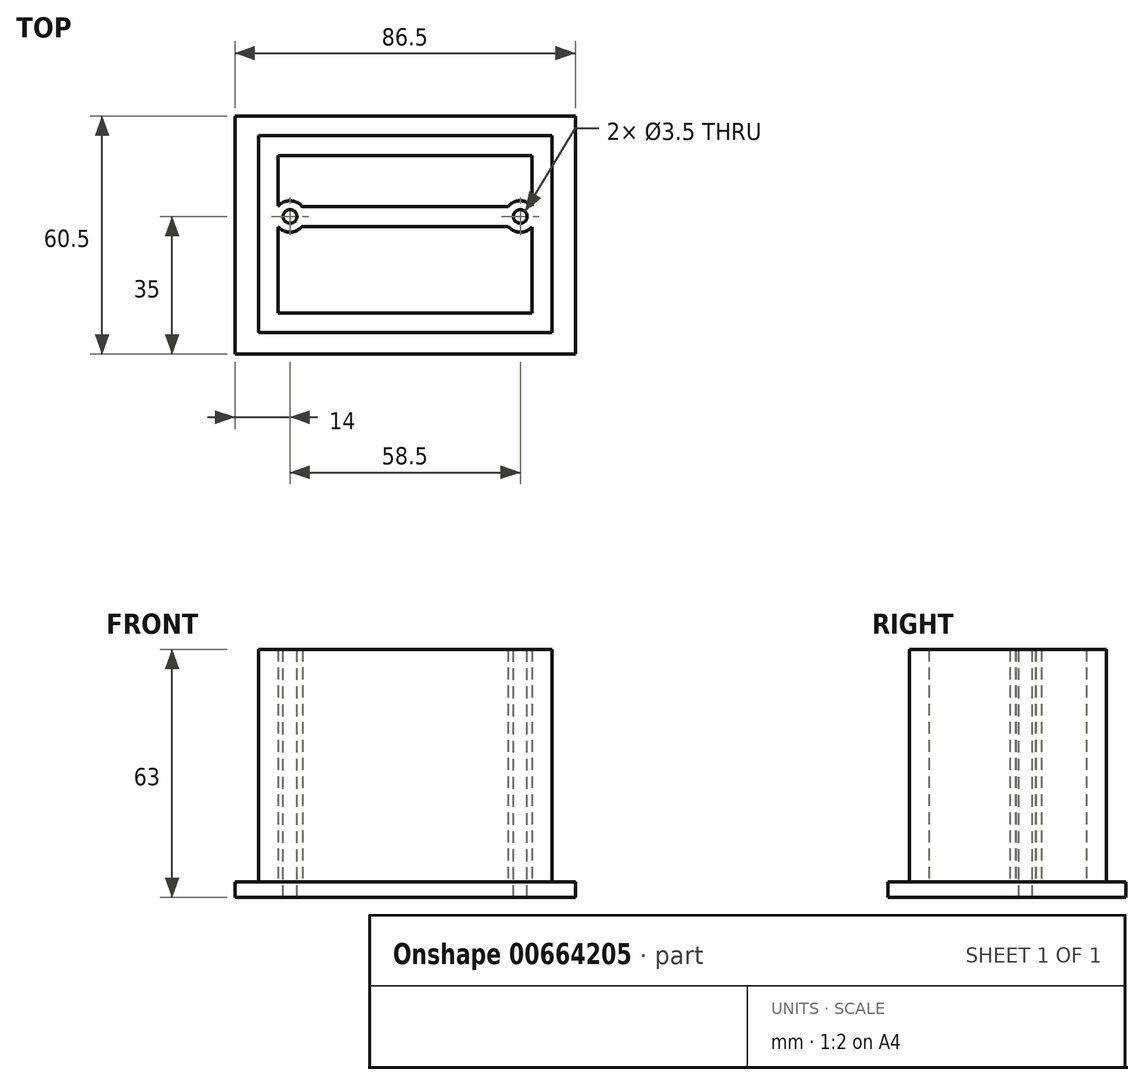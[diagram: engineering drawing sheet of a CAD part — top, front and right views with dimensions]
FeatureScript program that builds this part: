
annotation { "Feature Type Name" : "Feature", "Feature Type Description" : "" }
export const myFeature = defineFeature(function(context is Context, id is Id, definition is map)
    precondition{}
    {
        {
            var Q0;
            Q0=qCreatedBy(makeId("Top.planeOp"),FACE);
            var sketch = newSketch(context, id + "F0", { "sketchPlane" : qUnion([Q0])});
            skLineSegment(sketch, "E0.bottom", {"start": v(43.25, 30.25) * mm, "end": v(-43.25, 30.25) * mm});
            skLineSegment(sketch, "E0.top", {"start": v(43.25, -30.25) * mm, "end": v(-43.25, -30.25) * mm});
            skLineSegment(sketch, "E0.left", {"start": v(43.25, 30.25) * mm, "end": v(43.25, -30.25) * mm});
            skLineSegment(sketch, "E0.right", {"start": v(-43.25, 30.25) * mm, "end": v(-43.25, -30.25) * mm});
            skPoint(sketch, "E0.middle", {"position": v(0, 0) * mm});
            skSolve(sketch);
        }
        {
            var Q0;
            Q0=makeQuery(id+"F0.imprint","IMPRINT",FACE,{"disambiguationData":[TD([[makeQuery(id+"F0.imprint","IMPRINT",EDGE,{"derivedFrom":sQuery(id+"F0.wireOp",EDGE,"E0.bottom")}),1.0]])]});
            extrude(context, id + "F1", {"entities" : qUnion([Q0]), "depth" : 4 * mm, "offsetDistance" : 25 * mm});
        }
        {
            var Q0;
            Q0=makeQuery(id+"F1.opExtrude","CAP_FACE",FACE,{"disambiguationData":[OSD([sQuery(id+"F0.wireOp",EDGE,"E0.bottom"),sQuery(id+"F0.wireOp",EDGE,"E0.top"),sQuery(id+"F0.wireOp",EDGE,"E0.left"),sQuery(id+"F0.wireOp",EDGE,"E0.right")])],"isStart":false});
            var sketch = newSketch(context, id + "F2", { "sketchPlane" : qUnion([Q0])});
            skPoint(sketch, "E1.middle", {"position": v(0, 0) * mm});
            skArc(sketch, "E2", {"start": v(-26.13, 7.25) * mm, "mid": v(-29.15, 8.75) * mm, "end": v(-32.25, 7.4) * mm});
            skArc(sketch, "E3", {"start": v(26.13, 2.25) * mm, "mid": v(29.15, 0.75) * mm, "end": v(32.25, 2.1) * mm});
            skLineSegment(sketch, "E4.trimOffspring", {"start": v(-26.13, 7.25) * mm, "end": v(26.13, 7.25) * mm});
            skLineSegment(sketch, "E5.trimOffspring", {"start": v(-26.13, 2.25) * mm, "end": v(26.13, 2.25) * mm});
            skArc(sketch, "E6.trimOffspring", {"start": v(-32.25, 2.1) * mm, "mid": v(-29.15, 0.75) * mm, "end": v(-26.13, 2.25) * mm});
            skArc(sketch, "E7.trimOffspring", {"start": v(32.25, 7.4) * mm, "mid": v(29.15, 8.75) * mm, "end": v(26.13, 7.25) * mm});
            skLineSegment(sketch, "E8", {"start": v(-32.25, 7.4) * mm, "end": v(-32.25, 20.25) * mm});
            skLineSegment(sketch, "E9", {"start": v(-32.25, 20.25) * mm, "end": v(32.25, 20.25) * mm});
            skLineSegment(sketch, "E10", {"start": v(32.25, 20.25) * mm, "end": v(32.25, -19.75) * mm});
            skLineSegment(sketch, "E11", {"start": v(32.25, -19.75) * mm, "end": v(-32.25, -19.75) * mm});
            skLineSegment(sketch, "E12", {"start": v(-32.25, -19.75) * mm, "end": v(-32.25, 7.4) * mm});
            skLineSegment(sketch, "E13.0", {"start": v(37.25, 25.25) * mm, "end": v(37.25, -24.75) * mm});
            skLineSegment(sketch, "E13.1", {"start": v(-37.25, 25.25) * mm, "end": v(37.25, 25.25) * mm});
            skLineSegment(sketch, "E13.2", {"start": v(37.25, -24.75) * mm, "end": v(-37.25, -24.75) * mm});
            skLineSegment(sketch, "E13.3", {"start": v(-37.25, -24.75) * mm, "end": v(-37.25, 7.4) * mm});
            skLineSegment(sketch, "E13.4", {"start": v(-37.25, 7.4) * mm, "end": v(-37.25, 25.25) * mm});
            skSolve(sketch);
        }
        {
            var Q0;
            {var subQ1=sQuery(id+"F2.wireOp",EDGE,"E2");Q0=makeQuery(id+"F2.imprint","IMPRINT",FACE,{"disambiguationData":[TD([[makeQuery(id+"F2.imprint","IMPRINT",EDGE,{"derivedFrom":subQ1}),1.0]])]});}
            var Q1;
            {var subQ1=sQuery(id+"F2.wireOp",EDGE,"E8");Q1=makeQuery(id+"F2.imprint","IMPRINT",FACE,{"disambiguationData":[TD([[makeQuery(id+"F2.imprint","IMPRINT",EDGE,{"derivedFrom":subQ1}),1.0]])]});}
            extrude(context, id + "F3", {"entities" : qUnion([Q0, Q1]), "operationType" : NewBodyOperationType.ADD, "depth" : (121 - 62) * mm, "offsetDistance" : 25 * mm});
        }
        {
            var Q0;
            Q0=makeQuery(id+"F3.opExtrude","CAP_FACE",FACE,{"disambiguationData":[OSD([sQuery(id+"F2.wireOp",EDGE,"E1.bottom"),sQuery(id+"F2.wireOp",EDGE,"E1.top"),sQuery(id+"F2.wireOp",EDGE,"E1.left"),sQuery(id+"F2.wireOp",EDGE,"E1.right"),sQuery(id+"F2.wireOp",EDGE,"Kx9orHsY-sgCz-7O5J-Dl45-mCFPTs2FrGPJ.bottom"),sQuery(id+"F2.wireOp",EDGE,"Kx9orHsY-sgCz-7O5J-Dl45-mCFPTs2FrGPJ.top"),sQuery(id+"F2.wireOp",EDGE,"Kx9orHsY-sgCz-7O5J-Dl45-mCFPTs2FrGPJ.left"),sQuery(id+"F2.wireOp",EDGE,"Kx9orHsY-sgCz-7O5J-Dl45-mCFPTs2FrGPJ.right"),sQuery(id+"F2.wireOp",EDGE,"HYFIv0q8-FowS-Ntcz-HaLO-MFZJ2iC7tbck.bottom"),sQuery(id+"F2.wireOp",EDGE,"HYFIv0q8-FowS-Ntcz-HaLO-MFZJ2iC7tbck.top"),sQuery(id+"F2.wireOp",EDGE,"40449fd7-8b3a-4340-be27-2656412a8893.trimOffspring"),sQuery(id+"F2.wireOp",EDGE,"126be661-4c90-4f86-9ac7-4e1abece8fad.trimOffspring"),sQuery(id+"F2.wireOp",EDGE,"E2"),sQuery(id+"F2.wireOp",EDGE,"E3"),sQuery(id+"F2.wireOp",EDGE,"E4.trimOffspring"),sQuery(id+"F2.wireOp",EDGE,"E5.trimOffspring"),sQuery(id+"F2.wireOp",EDGE,"E6.trimOffspring"),sQuery(id+"F2.wireOp",EDGE,"1faa12ff-b82e-42e4-a45c-b0e4a6bedc49.trimOffspring"),sQuery(id+"F2.wireOp",EDGE,"4d0850c1-e95e-45d5-9ff1-f8f8371c6b59.trimOffspring"),sQuery(id+"F2.wireOp",EDGE,"E7.trimOffspring")])],"isStart":false});
            var sketch = newSketch(context, id + "F4", { "sketchPlane" : qUnion([Q0])});
            skCircle(sketch, "E14", {"center": v(-29.25, 4.75) * mm, "radius": 1.75 * mm});
            skCircle(sketch, "E15", {"center": v(29.25, 4.75) * mm, "radius": 1.75 * mm});
            skSolve(sketch);
        }
        {
            var Q0;
            Q0=makeQuery(id+"F4.imprint","IMPRINT",FACE,{"disambiguationData":[TD([[makeQuery(id+"F4.imprint","IMPRINT",EDGE,{"derivedFrom":sQuery(id+"F4.wireOp",EDGE,"E14")}),1.0]])]});
            var Q1;
            Q1=makeQuery(id+"F4.imprint","IMPRINT",FACE,{"disambiguationData":[TD([[makeQuery(id+"F4.imprint","IMPRINT",EDGE,{"derivedFrom":sQuery(id+"F4.wireOp",EDGE,"E15")}),1.0]])]});
            extrude(context, id + "F5", {"entities" : qUnion([Q0, Q1]), "operationType" : NewBodyOperationType.REMOVE, "endBound" : BoundingType.THROUGH_ALL, "oppositeDirection" : true, "depth" : 25 * mm, "offsetDistance" : 25 * mm});
        }
    });
